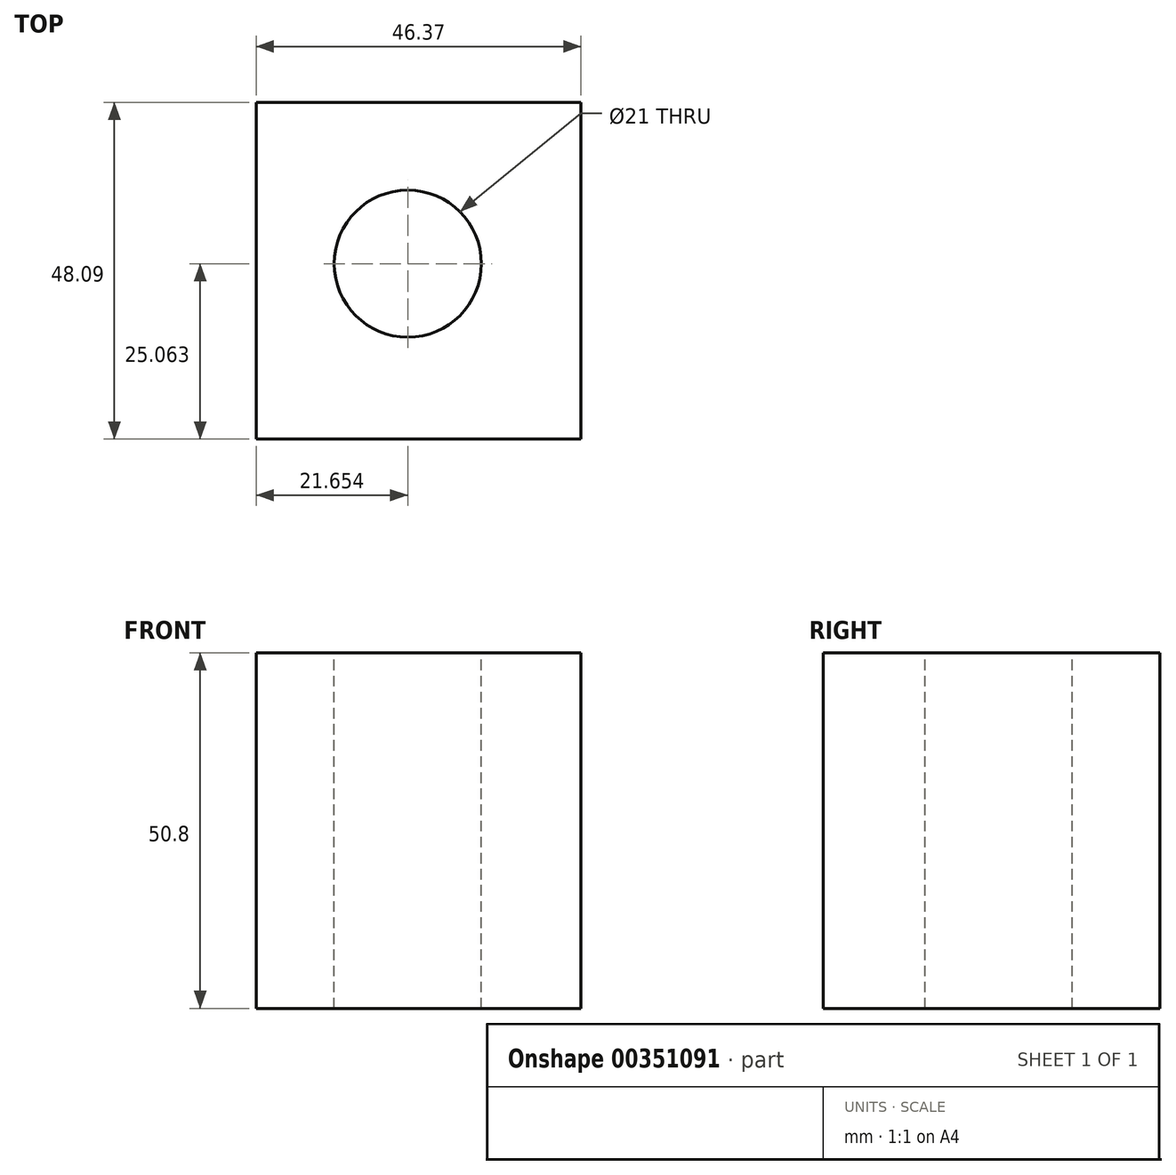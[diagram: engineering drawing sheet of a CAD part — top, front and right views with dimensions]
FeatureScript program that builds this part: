
annotation { "Feature Type Name" : "Feature", "Feature Type Description" : "" }
export const myFeature = defineFeature(function(context is Context, id is Id, definition is map)
    precondition{}
    {
        {
            var Q0;
            Q0=qCreatedBy(makeId("Top.planeOp"),FACE);
            var sketch = newSketch(context, id + "F0", { "sketchPlane" : qUnion([Q0])});
            skLineSegment(sketch, "E0.bottom", {"start": v(5.08, 0) * mm, "end": v(51.45, 0) * mm});
            skLineSegment(sketch, "E0.top", {"start": v(5.08, 48.09) * mm, "end": v(51.45, 48.09) * mm});
            skLineSegment(sketch, "E0.left", {"start": v(5.08, 0) * mm, "end": v(5.08, 48.09) * mm});
            skLineSegment(sketch, "E0.right", {"start": v(51.45, 0) * mm, "end": v(51.45, 48.09) * mm});
            skSolve(sketch);
        }
        {
            var Q0;
            Q0=makeQuery(id+"F0.imprint","IMPRINT",FACE,{"disambiguationData":[TD([[makeQuery(id+"F0.imprint","IMPRINT",EDGE,{"derivedFrom":sQuery(id+"F0.wireOp",EDGE,"E0.bottom")}),1.0]])]});
            extrude(context, id + "F1", {"entities" : qUnion([Q0]), "depth" : 50.8 * mm});
        }
        {
            var Q0;
            Q0=makeQuery(id+"F1.opExtrude","CAP_FACE",FACE,{"disambiguationData":[OSD([sQuery(id+"F0.wireOp",EDGE,"E0.bottom"),sQuery(id+"F0.wireOp",EDGE,"E0.top"),sQuery(id+"F0.wireOp",EDGE,"E0.left"),sQuery(id+"F0.wireOp",EDGE,"E0.right")])],"isStart":false});
            var sketch = newSketch(context, id + "F2", { "sketchPlane" : qUnion([Q0])});
            skPoint(sketch, "E1", {"position": v(26.73, 25.06) * mm});
            skSolve(sketch);
        }
        {
            var Q0;
            Q0=sQuery(id+"F2.wireOp",VERTEX,"E1");
            var Q1;
            Q1=makeQuery(id+"F1.opExtrude","SWEPT_BODY",BODY,{"disambiguationData":[OSD([sQuery(id+"F0.wireOp",EDGE,"E0.bottom"),sQuery(id+"F0.wireOp",EDGE,"E0.top"),sQuery(id+"F0.wireOp",EDGE,"E0.left"),sQuery(id+"F0.wireOp",EDGE,"E0.right")])]});
            hole(context, id + "F3", {"style" : HoleStyle.SIMPLE, "endStyle" : HoleEndStyle.THROUGH, "standardTappedOrClearance" : lookupTablePath({ "standard" : "ISO", "fit" : "Close", "size" : "M20", "type" : "Clearance" }), "standardBlindInLast" : lookupTablePath({ "fit" : "Close", "standard" : "ISO", "size" : "M20", "type" : "Clearance" }), "holeDiameter" : 21 * mm, "isTappedThrough" : true, "tappedDepth" : 12.7 * mm, "tapClearance" : 3, "locations" : qUnion([Q0]), "scope" : qUnion([Q1])});
        }
    });
